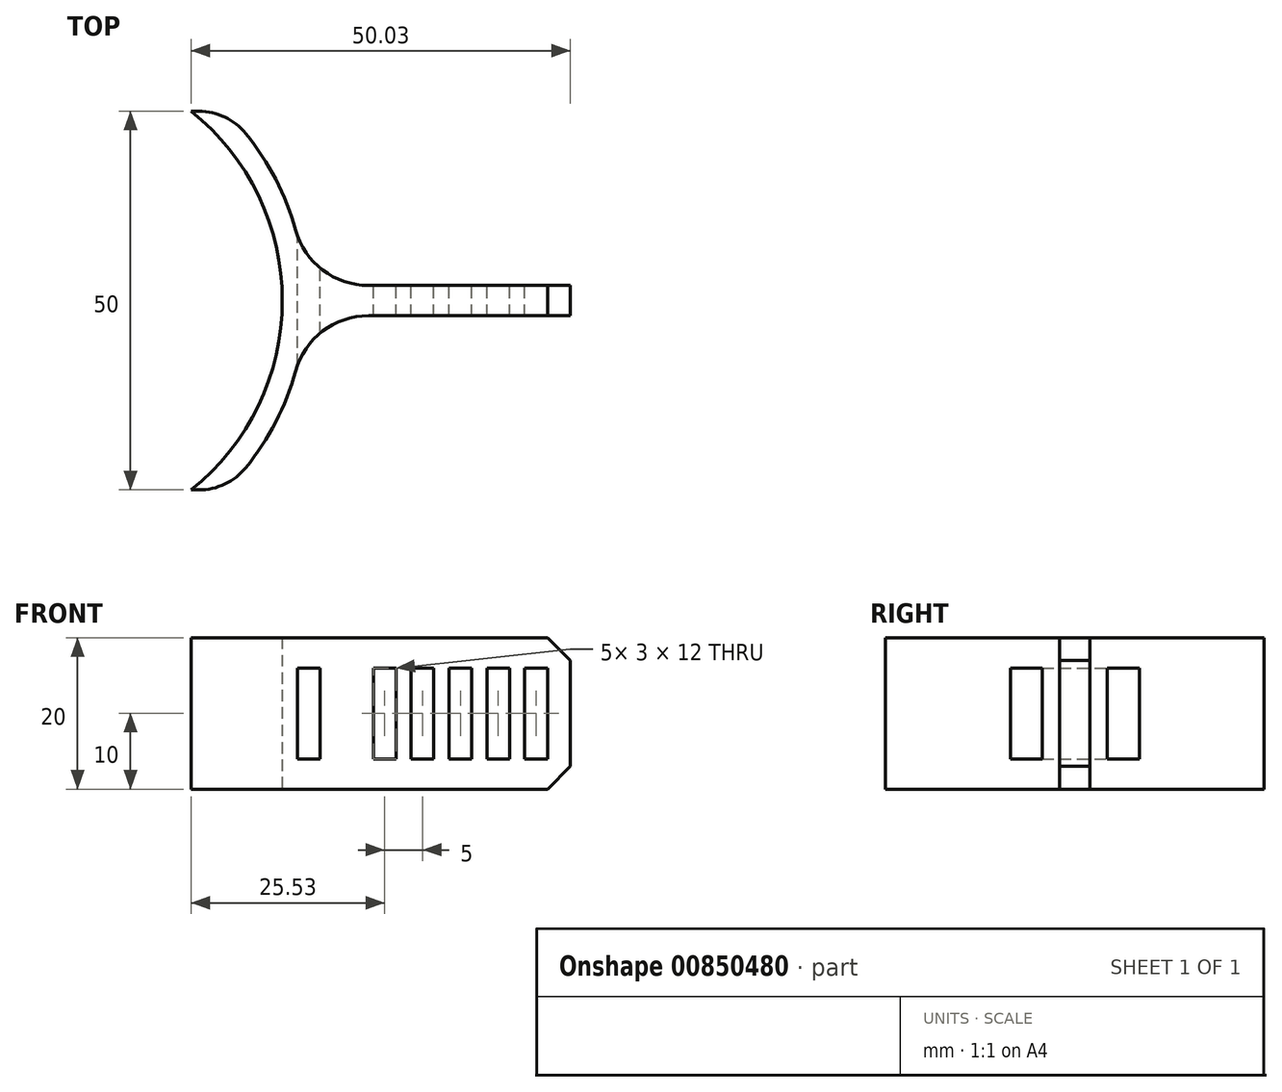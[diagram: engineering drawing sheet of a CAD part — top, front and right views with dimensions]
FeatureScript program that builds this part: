
annotation { "Feature Type Name" : "Feature", "Feature Type Description" : "" }
export const myFeature = defineFeature(function(context is Context, id is Id, definition is map)
    precondition{}
    {
        {
            var Q0;
            Q0=qCreatedBy(makeId("Top.planeOp"),FACE);
            var sketch = newSketch(context, id + "F0", { "sketchPlane" : qUnion([Q0])});
            skArc(sketch, "E0", {"start": v(33.73, 9.33) * mm, "mid": v(30.15, 17.78) * mm, "end": v(24.5, 25) * mm});
            skArc(sketch, "E1", {"start": v(19.97, -25) * mm, "mid": v(32, 0) * mm, "end": v(19.97, 25) * mm});
            skLineSegment(sketch, "E2", {"start": v(24.5, 25) * mm, "end": v(19.97, 25) * mm});
            skLineSegment(sketch, "E3", {"start": v(19.97, -25) * mm, "end": v(24.5, -25) * mm});
            skLineSegment(sketch, "E4.bottom", {"start": v(43.37, 2) * mm, "end": v(70, 2) * mm});
            skLineSegment(sketch, "E4.top", {"start": v(43.37, -2) * mm, "end": v(70, -2) * mm});
            skLineSegment(sketch, "E4.right", {"start": v(70, 2) * mm, "end": v(70, -2) * mm});
            skArc(sketch, "E5.filletArc", {"start": v(33.73, 9.33) * mm, "mid": v(37.32, 4.04) * mm, "end": v(43.37, 2) * mm});
            skArc(sketch, "E6", {"start": v(24.5, -25) * mm, "mid": v(30.15, -17.78) * mm, "end": v(33.73, -9.33) * mm});
            skArc(sketch, "E7.filletArc", {"start": v(43.37, -2) * mm, "mid": v(37.32, -4.04) * mm, "end": v(33.73, -9.33) * mm});
            skSolve(sketch);
        }
        {
            var Q0;
            Q0=makeQuery(id+"F0.imprint","IMPRINT",FACE,{"disambiguationData":[TD([[makeQuery(id+"F0.imprint","IMPRINT",EDGE,{"derivedFrom":sQuery(id+"F0.wireOp",EDGE,"E0")}),1.0]])]});
            extrude(context, id + "F1", {"entities" : qUnion([Q0]), "endBound" : BoundingType.SYMMETRIC, "depth" : 20 * mm, "offsetDistance" : 25 * mm});
        }
        {
            var Q0;
            Q0=qCreatedBy(makeId("Front.planeOp"),FACE);
            var sketch = newSketch(context, id + "F2", { "sketchPlane" : qUnion([Q0])});
            skLineSegment(sketch, "E8.bottom", {"start": v(34, 6) * mm, "end": v(37, 6) * mm});
            skLineSegment(sketch, "E8.top", {"start": v(34, -6) * mm, "end": v(37, -6) * mm});
            skLineSegment(sketch, "E8.left", {"start": v(34, 6) * mm, "end": v(34, -6) * mm});
            skLineSegment(sketch, "E8.right", {"start": v(37, 6) * mm, "end": v(37, -6) * mm});
            skLineSegment(sketch, "E9.bottom", {"start": v(59, 6) * mm, "end": v(62, 6) * mm});
            skLineSegment(sketch, "E9.top", {"start": v(59, -6) * mm, "end": v(62, -6) * mm});
            skLineSegment(sketch, "E9.left", {"start": v(59, 6) * mm, "end": v(59, -6) * mm});
            skLineSegment(sketch, "E9.right", {"start": v(62, 6) * mm, "end": v(62, -6) * mm});
            skLineSegment(sketch, "E10.bottom", {"start": v(54, 6) * mm, "end": v(57, 6) * mm});
            skLineSegment(sketch, "E10.top", {"start": v(54, -6) * mm, "end": v(57, -6) * mm});
            skLineSegment(sketch, "E10.left", {"start": v(54, 6) * mm, "end": v(54, -6) * mm});
            skLineSegment(sketch, "E10.right", {"start": v(57, 6) * mm, "end": v(57, -6) * mm});
            skLineSegment(sketch, "E11.bottom", {"start": v(49, 6) * mm, "end": v(52, 6) * mm});
            skLineSegment(sketch, "E11.top", {"start": v(49, -6) * mm, "end": v(52, -6) * mm});
            skLineSegment(sketch, "E11.left", {"start": v(49, 6) * mm, "end": v(49, -6) * mm});
            skLineSegment(sketch, "E11.right", {"start": v(52, 6) * mm, "end": v(52, -6) * mm});
            skLineSegment(sketch, "E12.bottom", {"start": v(64, 6) * mm, "end": v(67, 6) * mm});
            skLineSegment(sketch, "E12.top", {"start": v(64, -6) * mm, "end": v(67, -6) * mm});
            skLineSegment(sketch, "E12.left", {"start": v(64, 6) * mm, "end": v(64, -6) * mm});
            skLineSegment(sketch, "E12.right", {"start": v(67, 6) * mm, "end": v(67, -6) * mm});
            skLineSegment(sketch, "E13.bottom", {"start": v(44, 6) * mm, "end": v(47, 6) * mm});
            skLineSegment(sketch, "E13.top", {"start": v(44, -6) * mm, "end": v(47, -6) * mm});
            skLineSegment(sketch, "E13.left", {"start": v(44, 6) * mm, "end": v(44, -6) * mm});
            skLineSegment(sketch, "E13.right", {"start": v(47, 6) * mm, "end": v(47, -6) * mm});
            skSolve(sketch);
        }
        {
            var Q0;
            Q0=makeQuery(id+"F2.imprint","IMPRINT",FACE,{"disambiguationData":[TD([[makeQuery(id+"F2.imprint","IMPRINT",EDGE,{"derivedFrom":sQuery(id+"F2.wireOp",EDGE,"E12.bottom")}),-1.0]])]});
            var Q1;
            Q1=makeQuery(id+"F2.imprint","IMPRINT",FACE,{"disambiguationData":[TD([[makeQuery(id+"F2.imprint","IMPRINT",EDGE,{"derivedFrom":sQuery(id+"F2.wireOp",EDGE,"E13.bottom")}),-1.0]])]});
            var Q2;
            Q2=makeQuery(id+"F2.imprint","IMPRINT",FACE,{"disambiguationData":[TD([[makeQuery(id+"F2.imprint","IMPRINT",EDGE,{"derivedFrom":sQuery(id+"F2.wireOp",EDGE,"E11.bottom")}),-1.0]])]});
            var Q3;
            Q3=makeQuery(id+"F2.imprint","IMPRINT",FACE,{"disambiguationData":[TD([[makeQuery(id+"F2.imprint","IMPRINT",EDGE,{"derivedFrom":sQuery(id+"F2.wireOp",EDGE,"E9.bottom")}),-1.0]])]});
            var Q4;
            Q4=makeQuery(id+"F2.imprint","IMPRINT",FACE,{"disambiguationData":[TD([[makeQuery(id+"F2.imprint","IMPRINT",EDGE,{"derivedFrom":sQuery(id+"F2.wireOp",EDGE,"E10.bottom")}),-1.0]])]});
            var Q5;
            Q5=makeQuery(id+"F2.imprint","IMPRINT",FACE,{"disambiguationData":[TD([[makeQuery(id+"F2.imprint","IMPRINT",EDGE,{"derivedFrom":sQuery(id+"F2.wireOp",EDGE,"E8.bottom")}),-1.0]])]});
            extrude(context, id + "F3", {"entities" : qUnion([Q0, Q1, Q2, Q3, Q4, Q5]), "endBound" : BoundingType.SYMMETRIC, "depth" : 20 * mm, "offsetDistance" : 25 * mm});
        }
        {
            var Q0;
            Q0=makeQuery(id+"F3.opExtrude","SWEPT_BODY",BODY,{"disambiguationData":[OSD([sQuery(id+"F2.wireOp",EDGE,"E8.bottom"),sQuery(id+"F2.wireOp",EDGE,"E8.top"),sQuery(id+"F2.wireOp",EDGE,"E8.left"),sQuery(id+"F2.wireOp",EDGE,"E8.right")])]});
            var Q1;
            Q1=makeQuery(id+"F3.opExtrude","SWEPT_BODY",BODY,{"disambiguationData":[OSD([sQuery(id+"F2.wireOp",EDGE,"E13.bottom"),sQuery(id+"F2.wireOp",EDGE,"E13.top"),sQuery(id+"F2.wireOp",EDGE,"E13.left"),sQuery(id+"F2.wireOp",EDGE,"E13.right")])]});
            var Q2;
            Q2=makeQuery(id+"F3.opExtrude","SWEPT_BODY",BODY,{"disambiguationData":[OSD([sQuery(id+"F2.wireOp",EDGE,"E11.bottom"),sQuery(id+"F2.wireOp",EDGE,"E11.top"),sQuery(id+"F2.wireOp",EDGE,"E11.left"),sQuery(id+"F2.wireOp",EDGE,"E11.right")])]});
            var Q3;
            Q3=makeQuery(id+"F3.opExtrude","SWEPT_BODY",BODY,{"disambiguationData":[OSD([sQuery(id+"F2.wireOp",EDGE,"E10.bottom"),sQuery(id+"F2.wireOp",EDGE,"E10.top"),sQuery(id+"F2.wireOp",EDGE,"E10.left"),sQuery(id+"F2.wireOp",EDGE,"E10.right")])]});
            var Q4;
            Q4=makeQuery(id+"F3.opExtrude","SWEPT_BODY",BODY,{"disambiguationData":[OSD([sQuery(id+"F2.wireOp",EDGE,"E9.bottom"),sQuery(id+"F2.wireOp",EDGE,"E9.top"),sQuery(id+"F2.wireOp",EDGE,"E9.left"),sQuery(id+"F2.wireOp",EDGE,"E9.right")])]});
            var Q5;
            Q5=makeQuery(id+"F3.opExtrude","SWEPT_BODY",BODY,{"disambiguationData":[OSD([sQuery(id+"F2.wireOp",EDGE,"E12.bottom"),sQuery(id+"F2.wireOp",EDGE,"E12.top"),sQuery(id+"F2.wireOp",EDGE,"E12.left"),sQuery(id+"F2.wireOp",EDGE,"E12.right")])]});
            var Q6;
            Q6=makeQuery(id+"F1.opExtrude","SWEPT_BODY",BODY,{"disambiguationData":[OSD([sQuery(id+"F0.wireOp",EDGE,"E0"),sQuery(id+"F0.wireOp",EDGE,"E1"),sQuery(id+"F0.wireOp",EDGE,"E2"),sQuery(id+"F0.wireOp",EDGE,"E3"),sQuery(id+"F0.wireOp",EDGE,"E4.bottom"),sQuery(id+"F0.wireOp",EDGE,"E4.top"),sQuery(id+"F0.wireOp",EDGE,"E4.right"),sQuery(id+"F0.wireOp",EDGE,"E5.filletArc"),sQuery(id+"F0.wireOp",EDGE,"E6"),sQuery(id+"F0.wireOp",EDGE,"E7.filletArc")])]});
            booleanBodies(context, id + "F4", {"operationType" : BooleanOperationType.SUBTRACTION, "tools" : qUnion([Q0, Q1, Q2, Q3, Q4, Q5]), "targets" : qUnion([Q6])});
        }
        {
            var Q0;
            Q0=makeQuery(id+"F1.opExtrude","CAP_EDGE",EDGE,{"disambiguationData":[OSD([sQuery(id+"F0.wireOp",EDGE,"E4.right")])],"isStart":false});
            var Q1;
            Q1=makeQuery(id+"F1.opExtrude","CAP_EDGE",EDGE,{"disambiguationData":[OSD([sQuery(id+"F0.wireOp",EDGE,"E4.right")])],"isStart":true});
            chamfer(context, id + "F5", {"entities" : qUnion([Q0, Q1]), "width" : 3 * mm, "tangentPropagation" : true});
        }
        {
            var Q0;
            Q0=makeQuery(id+"F1.opExtrude","SWEPT_EDGE",EDGE,{"disambiguationData":[OSD([sQuery(id+"F0.wireOp",EDGE,"E0"),sQuery(id+"F0.wireOp",EDGE,"E2")])]});
            var Q1;
            Q1=makeQuery(id+"F1.opExtrude","SWEPT_EDGE",EDGE,{"disambiguationData":[OSD([sQuery(id+"F0.wireOp",EDGE,"E3"),sQuery(id+"F0.wireOp",EDGE,"E6")])]});
            fillet(context, id + "F6", {"entities" : qUnion([Q0, Q1]), "radius" : 8 * mm, "tangentPropagation" : true, "allowEdgeOverflow" : false});
        }
    });
